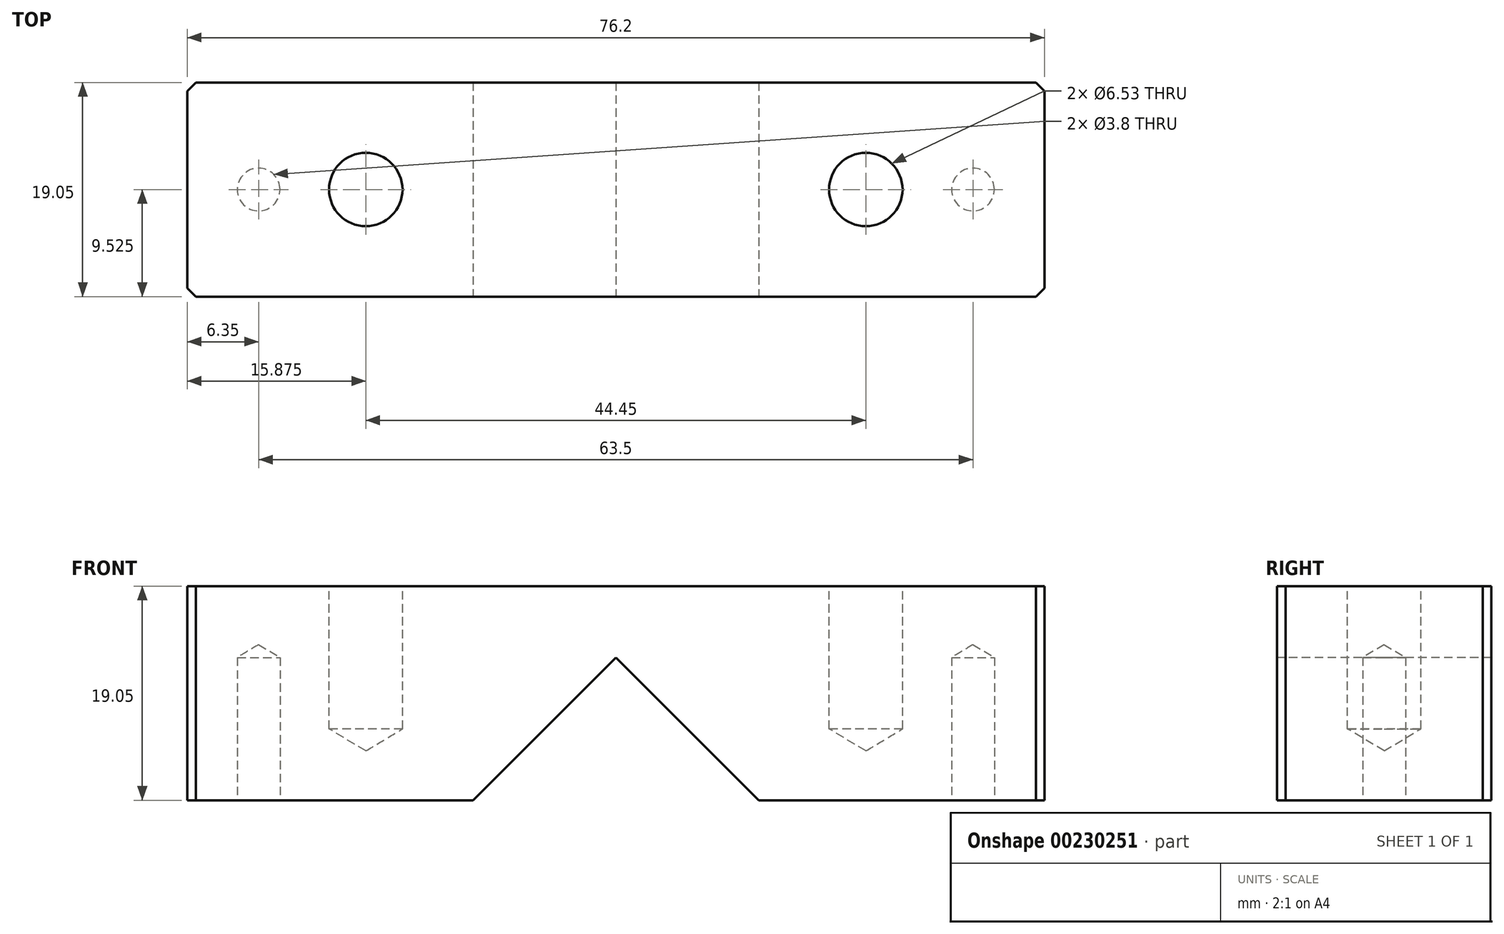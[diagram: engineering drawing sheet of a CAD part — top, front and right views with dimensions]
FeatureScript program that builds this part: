
annotation { "Feature Type Name" : "Feature", "Feature Type Description" : "" }
export const myFeature = defineFeature(function(context is Context, id is Id, definition is map)
    precondition{}
    {
        {
            var Q0;
            Q0=qCreatedBy(makeId("Right.planeOp"),FACE);
            var sketch = newSketch(context, id + "F0", { "sketchPlane" : qUnion([Q0])});
            skLineSegment(sketch, "E0.bottom", {"start": v(0, 0) * mm, "end": v(-19.05, 0) * mm});
            skLineSegment(sketch, "E0.top", {"start": v(0, 19.05) * mm, "end": v(-19.05, 19.05) * mm});
            skLineSegment(sketch, "E0.left", {"start": v(0, 0) * mm, "end": v(0, 19.05) * mm});
            skLineSegment(sketch, "E0.right", {"start": v(-19.05, 0) * mm, "end": v(-19.05, 19.05) * mm});
            skSolve(sketch);
        }
        {
            var Q0;
            Q0 = qSketchRegion(id + "F0", true);
            extrude(context, id + "F1", {"entities" : qUnion([Q0]), "depth" : 76.2 * mm});
        }
        {
            var Q0;
            Q0=makeQuery(id+"F1.opExtrude","SWEPT_FACE",FACE,{"disambiguationData":[OSD([sQuery(id+"F0.wireOp",EDGE,"E0.right")])]});
            var sketch = newSketch(context, id + "F2", { "sketchPlane" : qUnion([Q0])});
            skLineSegment(sketch, "E1", {"start": v(38.1, 19.05) * mm, "end": v(38.1, -17.96) * mm});
            skCircle(sketch, "E2", {"center": v(38.1, -5.26) * mm, "radius": 12.7 * mm, "construction": true});
            skPoint(sketch, "E2.second.point", {"position": v(38.1, 7.44) * mm});
            skPoint(sketch, "E2.third.point", {"position": v(25.48, -6.68) * mm});
            skLineSegment(sketch, "E3", {"start": v(25.4, 0) * mm, "end": v(38.1, 12.7) * mm});
            skLineSegment(sketch, "E4", {"start": v(38.1, 12.7) * mm, "end": v(50.8, 0) * mm});
            skLineSegment(sketch, "E5", {"start": v(25.4, 0) * mm, "end": v(50.8, 0) * mm});
            skSolve(sketch);
        }
        {
            var Q0;
            Q0 = qSketchRegion(id + "F2", true);
            extrude(context, id + "F3", {"entities" : qUnion([Q0]), "operationType" : NewBodyOperationType.REMOVE, "oppositeDirection" : true, "depth" : 25.4 * mm});
        }
        {
            var Q0;
            Q0=makeQuery(id+"F1.opExtrude","SWEPT_FACE",FACE,{"disambiguationData":[OSD([sQuery(id+"F0.wireOp",EDGE,"E0.top")])]});
            var sketch = newSketch(context, id + "F4", { "sketchPlane" : qUnion([Q0])});
            skLineSegment(sketch, "E6", {"start": v(76.2, -9.53) * mm, "end": v(60.33, -9.53) * mm});
            skPoint(sketch, "E7", {"position": v(60.33, -9.53) * mm});
            skLineSegment(sketch, "E8", {"start": v(76.2, -9.53) * mm, "end": v(15.88, -9.53) * mm});
            skPoint(sketch, "E9", {"position": v(15.88, -9.53) * mm});
            skSolve(sketch);
        }
        {
            var Q0;
            Q0=sQuery(id+"F4.wireOp",VERTEX,"E9");
            var Q1;
            Q1=sQuery(id+"F4.wireOp",VERTEX,"E7");
            var Q2;
            Q2=makeQuery(id+"F1.opExtrude","SWEPT_BODY",BODY,{"disambiguationData":[OSD([sQuery(id+"F0.wireOp",EDGE,"E0.bottom"),sQuery(id+"F0.wireOp",EDGE,"E0.top"),sQuery(id+"F0.wireOp",EDGE,"E0.left"),sQuery(id+"F0.wireOp",EDGE,"E0.right")])]});
            hole(context, id + "F5", {"style" : HoleStyle.SIMPLE, "endStyle" : HoleEndStyle.BLIND, "standardTappedOrClearance" : lookupTablePath({ "standard" : "ANSI", "engagement" : "75%", "pitch" : "18 tpi", "size" : "5/16", "type" : "Tapped" }), "standardBlindInLast" : lookupTablePath({ "standard" : "ANSI", "engagement" : "75%", "pitch" : "18 tpi", "size" : "5/16", "type" : "Tapped" }), "holeDiameter" : 6.53 * mm, "holeDepth" : 12.7 * mm, "locations" : qUnion([Q0, Q1]), "scope" : qUnion([Q2]), "majorDiameter" : 7.94 * mm});
        }
        {
            var Q0;
            {var subQ2=sQuery(id+"F0.wireOp",EDGE,"E0.bottom");Q0=makeQuery(id+"F3.boolean.opBoolean","SPLIT",FACE,{"disambiguationData":[TD([makeQuery(id+"F3.opExtrude","SWEPT_FACE",FACE,{"disambiguationData":[OSD([sQuery(id+"F2.wireOp",EDGE,"E4")])]})])],"derivedFrom":makeQuery(id+"F1.opExtrude","SWEPT_FACE",FACE,{"disambiguationData":[OSD([subQ2])]})});}
            var sketch = newSketch(context, id + "F6", { "sketchPlane" : qUnion([Q0])});
            skLineSegment(sketch, "E10", {"start": v(76.2, 9.53) * mm, "end": v(69.85, 9.53) * mm});
            skLineSegment(sketch, "E11", {"start": v(69.85, 9.53) * mm, "end": v(6.35, 9.53) * mm});
            skPoint(sketch, "E12", {"position": v(6.35, 9.53) * mm});
            skPoint(sketch, "E13", {"position": v(69.85, 9.53) * mm});
            skSolve(sketch);
        }
        {
            var Q0;
            Q0=sQuery(id+"F6.wireOp",VERTEX,"E12");
            var Q1;
            Q1=sQuery(id+"F6.wireOp",VERTEX,"E13");
            var Q2;
            Q2=makeQuery(id+"F1.opExtrude","SWEPT_BODY",BODY,{"disambiguationData":[OSD([sQuery(id+"F0.wireOp",EDGE,"E0.bottom"),sQuery(id+"F0.wireOp",EDGE,"E0.top"),sQuery(id+"F0.wireOp",EDGE,"E0.left"),sQuery(id+"F0.wireOp",EDGE,"E0.right")])]});
            hole(context, id + "F7", {"style" : HoleStyle.SIMPLE, "endStyle" : HoleEndStyle.BLIND, "standardTappedOrClearance" : lookupTablePath({ "standard" : "ANSI", "engagement" : "75%", "pitch" : "24 tpi", "size" : "#10", "type" : "Tapped" }), "standardBlindInLast" : lookupTablePath({ "standard" : "ANSI", "engagement" : "75%", "pitch" : "24 tpi", "size" : "#10", "type" : "Tapped" }), "holeDiameter" : 3.8 * mm, "holeDepth" : 12.7 * mm, "locations" : qUnion([Q0, Q1]), "scope" : qUnion([Q2]), "majorDiameter" : 4.83 * mm});
        }
        {
            var Q0;
            Q0=makeQuery(id+"F1.opExtrude","CAP_EDGE",EDGE,{"disambiguationData":[OSD([sQuery(id+"F0.wireOp",EDGE,"E0.right")])],"isStart":false});
            var Q1;
            Q1=makeQuery(id+"F1.opExtrude","CAP_EDGE",EDGE,{"disambiguationData":[OSD([sQuery(id+"F0.wireOp",EDGE,"E0.left")])],"isStart":false});
            var Q2;
            Q2=makeQuery(id+"F1.opExtrude","CAP_EDGE",EDGE,{"disambiguationData":[OSD([sQuery(id+"F0.wireOp",EDGE,"E0.right")])],"isStart":true});
            var Q3;
            Q3=makeQuery(id+"F1.opExtrude","CAP_EDGE",EDGE,{"disambiguationData":[OSD([sQuery(id+"F0.wireOp",EDGE,"E0.left")])],"isStart":true});
            chamfer(context, id + "F8", {"entities" : qUnion([Q0, Q1, Q2, Q3]), "chamferType" : ChamferType.OFFSET_ANGLE, "width" : 0.76 * mm, "oppositeDirection" : false, "angle" : 45 * degree, "tangentPropagation" : true});
        }
    });
